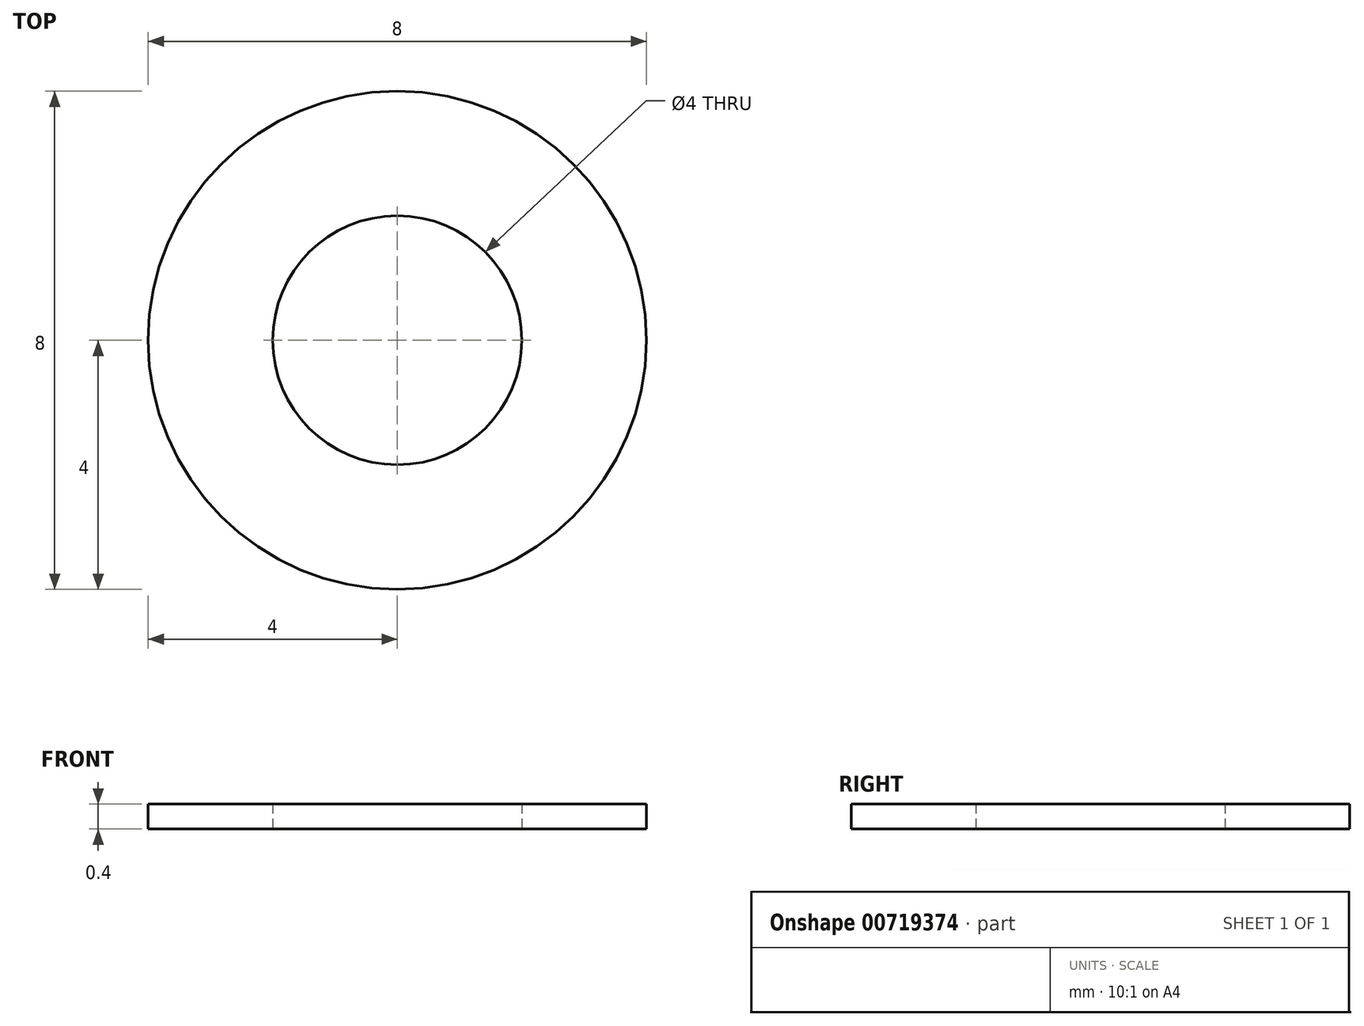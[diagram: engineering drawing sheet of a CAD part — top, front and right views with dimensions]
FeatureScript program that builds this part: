
annotation { "Feature Type Name" : "Feature", "Feature Type Description" : "" }
export const myFeature = defineFeature(function(context is Context, id is Id, definition is map)
    precondition{}
    {
        {
            var Q0;
            Q0=qCreatedBy(makeId("Top.planeOp"),FACE);
            var sketch = newSketch(context, id + "F0", { "sketchPlane" : qUnion([Q0])});
            skCircle(sketch, "E0", {"center": v(0, 0) * mm, "radius": 2 * mm});
            skCircle(sketch, "E1", {"center": v(0, 0) * mm, "radius": 4 * mm});
            skSolve(sketch);
        }
        {
            var Q0;
            Q0 = qSketchRegion(id + "F0", true);
            extrude(context, id + "F1", {"entities" : qUnion([Q0]), "depth" : 0.4 * mm, "offsetDistance" : 25.4 * mm});
        }
    });
